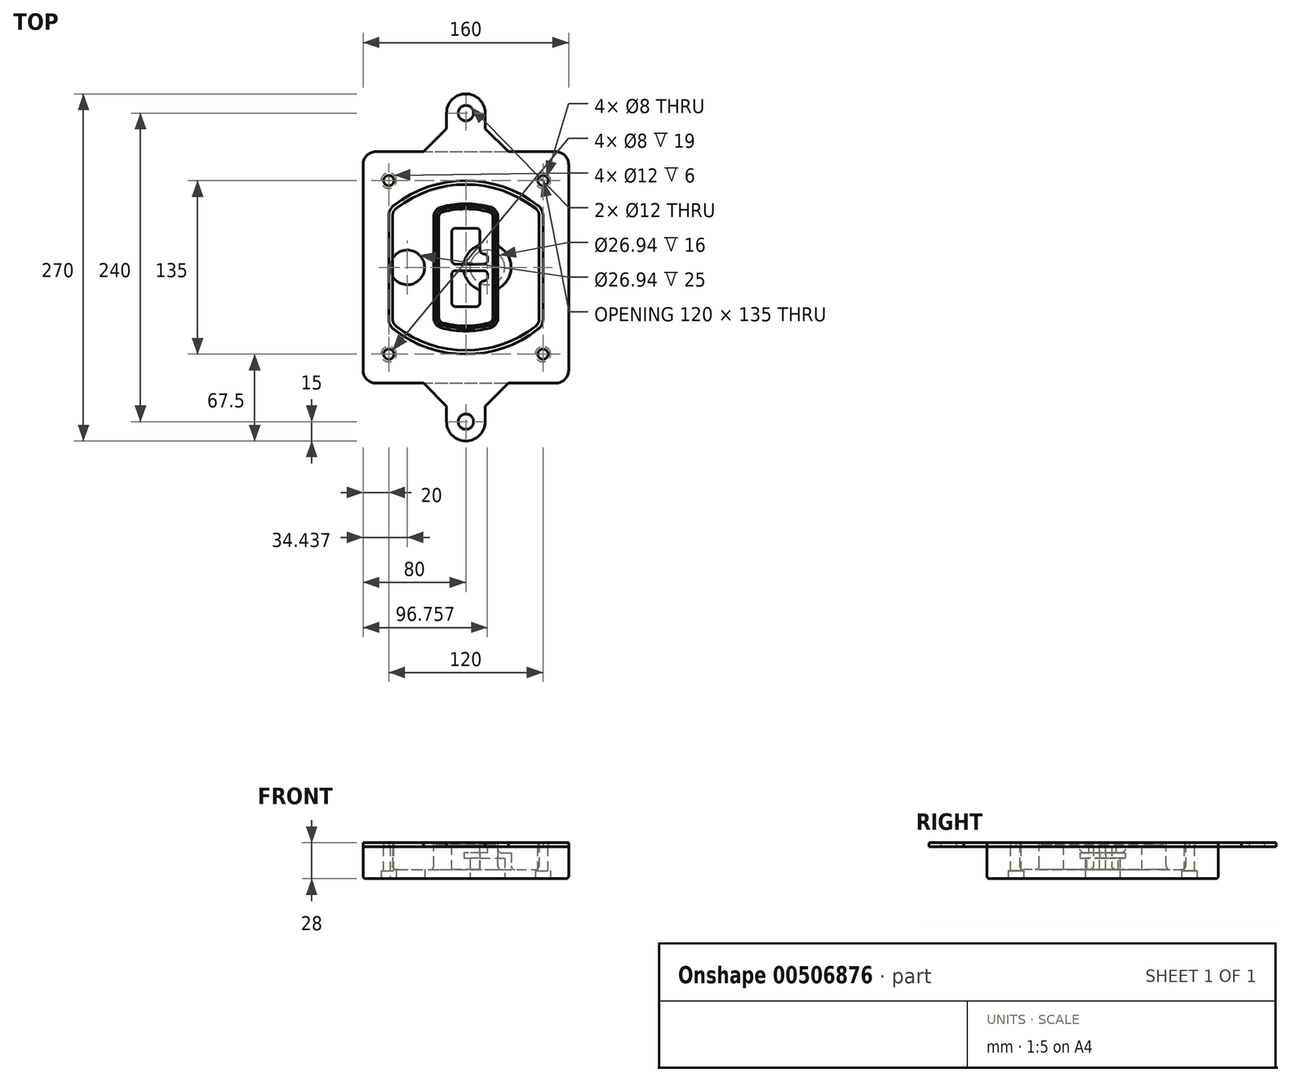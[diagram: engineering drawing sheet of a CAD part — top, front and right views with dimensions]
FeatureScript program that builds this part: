
annotation { "Feature Type Name" : "Feature", "Feature Type Description" : "" }
export const myFeature = defineFeature(function(context is Context, id is Id, definition is map)
    precondition{}
    {
        {
            var Q0;
            Q0=qCreatedBy(makeId("Top.planeOp"),FACE);
            var sketch = newSketch(context, id + "F0", { "sketchPlane" : qUnion([Q0])});
            skPoint(sketch, "E0.rect.middle", {"position": v(0, 0) * mm});
            skLineSegment(sketch, "E1.bottom", {"start": v(-70, -90) * mm, "end": v(70, -90) * mm});
            skLineSegment(sketch, "E1.top", {"start": v(-70, 90) * mm, "end": v(70, 90) * mm});
            skLineSegment(sketch, "E1.left", {"start": v(-80, -80) * mm, "end": v(-80, 80) * mm});
            skLineSegment(sketch, "E1.right", {"start": v(80, -80) * mm, "end": v(80, 80) * mm});
            skLineSegment(sketch, "E2", {"start": v(-80, 90) * mm, "end": v(80, -90) * mm, "construction": true});
            skLineSegment(sketch, "E3", {"start": v(80, 90) * mm, "end": v(-80, -90) * mm, "construction": true});
            skCircle(sketch, "E4", {"center": v(-60, 67.5) * mm, "radius": 4 * mm});
            skCircle(sketch, "E5", {"center": v(60, 67.5) * mm, "radius": 4 * mm});
            skCircle(sketch, "E6", {"center": v(60, -67.5) * mm, "radius": 4 * mm});
            skCircle(sketch, "E7", {"center": v(-60, -67.5) * mm, "radius": 4 * mm});
            skLineSegment(sketch, "E8", {"start": v(-60, 67.5) * mm, "end": v(60, 67.5) * mm, "construction": true});
            skLineSegment(sketch, "E9", {"start": v(60, 67.5) * mm, "end": v(60, -67.5) * mm, "construction": true});
            skLineSegment(sketch, "E10", {"start": v(60, -67.5) * mm, "end": v(-60, -67.5) * mm, "construction": true});
            skLineSegment(sketch, "E11", {"start": v(-60, -67.5) * mm, "end": v(-60, 67.5) * mm, "construction": true});
            skLineSegment(sketch, "E12", {"start": v(-60, 40.3) * mm, "end": v(-60, -40.3) * mm});
            skLineSegment(sketch, "E13", {"start": v(60, 40.3) * mm, "end": v(60, -40.3) * mm});
            skArc(sketch, "E14", {"start": v(56.15, 48.18) * mm, "mid": v(0, 67.5) * mm, "end": v(-56.15, 48.18) * mm});
            skArc(sketch, "E15", {"start": v(-56.15, -48.18) * mm, "mid": v(0, -67.5) * mm, "end": v(56.15, -48.18) * mm});
            skLineSegment(sketch, "E16", {"start": v(-60, 0) * mm, "end": v(60, 0) * mm, "construction": true});
            skPoint(sketch, "E17.visualSharp", {"position": v(-60, -45) * mm});
            skArc(sketch, "E17.filletArc", {"start": v(-60, -40.3) * mm, "mid": v(-58.99, -44.68) * mm, "end": v(-56.15, -48.18) * mm});
            skPoint(sketch, "E18.visualSharp", {"position": v(-60, 45) * mm});
            skArc(sketch, "E18.filletArc", {"start": v(-56.15, 48.18) * mm, "mid": v(-58.99, 44.68) * mm, "end": v(-60, 40.3) * mm});
            skPoint(sketch, "E19.visualSharp", {"position": v(60, 45) * mm});
            skArc(sketch, "E19.filletArc", {"start": v(60, 40.3) * mm, "mid": v(58.99, 44.68) * mm, "end": v(56.15, 48.18) * mm});
            skPoint(sketch, "E20.visualSharp", {"position": v(60, -45) * mm});
            skArc(sketch, "E20.filletArc", {"start": v(56.15, -48.18) * mm, "mid": v(58.99, -44.68) * mm, "end": v(60, -40.3) * mm});
            skPoint(sketch, "E21.visualSharp", {"position": v(-80, 90) * mm});
            skArc(sketch, "E21.filletArc", {"start": v(-70, 90) * mm, "mid": v(-77.07, 87.07) * mm, "end": v(-80, 80) * mm});
            skPoint(sketch, "E22.visualSharp", {"position": v(80, 90) * mm});
            skArc(sketch, "E22.filletArc", {"start": v(80, 80) * mm, "mid": v(77.07, 87.07) * mm, "end": v(70, 90) * mm});
            skPoint(sketch, "E23.visualSharp", {"position": v(80, -90) * mm});
            skArc(sketch, "E23.filletArc", {"start": v(70, -90) * mm, "mid": v(77.07, -87.07) * mm, "end": v(80, -80) * mm});
            skPoint(sketch, "E24.visualSharp", {"position": v(-80, -90) * mm});
            skArc(sketch, "E24.filletArc", {"start": v(-80, -80) * mm, "mid": v(-77.07, -87.07) * mm, "end": v(-70, -90) * mm});
            skArc(sketch, "E25.0", {"start": v(57, 40.3) * mm, "mid": v(56.3, 43.36) * mm, "end": v(54.3, 45.81) * mm});
            skLineSegment(sketch, "E25.1", {"start": v(57, 40.3) * mm, "end": v(57, -40.3) * mm});
            skArc(sketch, "E25.2", {"start": v(54.3, -45.81) * mm, "mid": v(56.3, -43.36) * mm, "end": v(57, -40.3) * mm});
            skArc(sketch, "E25.3", {"start": v(-54.3, -45.81) * mm, "mid": v(0, -64.5) * mm, "end": v(54.3, -45.81) * mm});
            skArc(sketch, "E25.4", {"start": v(-57, -40.3) * mm, "mid": v(-56.3, -43.36) * mm, "end": v(-54.3, -45.81) * mm});
            skArc(sketch, "E25.5", {"start": v(54.3, 45.81) * mm, "mid": v(0, 64.5) * mm, "end": v(-54.3, 45.81) * mm});
            skLineSegment(sketch, "E25.6", {"start": v(-57, 40.3) * mm, "end": v(-57, -40.3) * mm});
            skArc(sketch, "E25.7", {"start": v(-54.3, 45.81) * mm, "mid": v(-56.3, 43.36) * mm, "end": v(-57, 40.3) * mm});
            skArc(sketch, "E26.0", {"start": v(-58.62, 51.33) * mm, "mid": v(-62.58, 46.43) * mm, "end": v(-64, 40.3) * mm});
            skArc(sketch, "E26.1", {"start": v(58.62, 51.33) * mm, "mid": v(0, 71.5) * mm, "end": v(-58.62, 51.33) * mm});
            skArc(sketch, "E26.2", {"start": v(64, 40.3) * mm, "mid": v(62.58, 46.43) * mm, "end": v(58.62, 51.33) * mm});
            skLineSegment(sketch, "E26.3", {"start": v(64, 40.3) * mm, "end": v(64, -40.3) * mm});
            skArc(sketch, "E26.4", {"start": v(58.62, -51.33) * mm, "mid": v(62.58, -46.43) * mm, "end": v(64, -40.3) * mm});
            skLineSegment(sketch, "E26.5", {"start": v(-64, 40.3) * mm, "end": v(-64, -40.3) * mm});
            skArc(sketch, "E26.6", {"start": v(-58.62, -51.33) * mm, "mid": v(0, -71.5) * mm, "end": v(58.62, -51.33) * mm});
            skArc(sketch, "E26.7", {"start": v(-64, -40.3) * mm, "mid": v(-62.58, -46.43) * mm, "end": v(-58.62, -51.33) * mm});
            skSolve(sketch);
        }
        {
            var Q0;
            Q0=makeQuery(id+"F0.imprint","IMPRINT",FACE,{"disambiguationData":[TD([[makeQuery(id+"F0.imprint","IMPRINT",EDGE,{"derivedFrom":sQuery(id+"F0.wireOp",EDGE,"E1.bottom")}),1.0]])]});
            var Q1;
            Q1=makeQuery(id+"F0.imprint","IMPRINT",FACE,{"disambiguationData":[TD([[makeQuery(id+"F0.imprint","IMPRINT",EDGE,{"derivedFrom":sQuery(id+"F0.wireOp",EDGE,"E12")}),1.0]])]});
            var Q2;
            Q2=makeQuery(id+"F0.imprint","IMPRINT",FACE,{"disambiguationData":[TD([[makeQuery(id+"F0.imprint","IMPRINT",EDGE,{"derivedFrom":sQuery(id+"F0.wireOp",EDGE,"E25.0")}),1.0]])]});
            var Q3;
            Q3=makeQuery(id+"F0.imprint","IMPRINT",FACE,{"disambiguationData":[TD([[makeQuery(id+"F0.imprint","IMPRINT",EDGE,{"derivedFrom":sQuery(id+"F0.wireOp",EDGE,"E12")}),-1.0]])]});
            extrude(context, id + "F1", {"entities" : qUnion([Q0, Q1, Q2, Q3]), "oppositeDirection" : true, "depth" : 25 * mm});
        }
        {
            var Q0;
            Q0=makeQuery(id+"F0.imprint","IMPRINT",FACE,{"disambiguationData":[TD([[makeQuery(id+"F0.imprint","IMPRINT",EDGE,{"derivedFrom":sQuery(id+"F0.wireOp",EDGE,"E12")}),1.0]])]});
            extrude(context, id + "F2", {"entities" : qUnion([Q0]), "operationType" : NewBodyOperationType.ADD, "depth" : 3 * mm});
        }
        {
            var Q0;
            Q0=makeQuery(id+"F0.imprint","IMPRINT",FACE,{"disambiguationData":[TD([[makeQuery(id+"F0.imprint","IMPRINT",EDGE,{"derivedFrom":sQuery(id+"F0.wireOp",EDGE,"E25.0")}),1.0]])]});
            extrude(context, id + "F3", {"entities" : qUnion([Q0]), "operationType" : NewBodyOperationType.REMOVE, "oppositeDirection" : true, "depth" : 18 * mm});
        }
        {
            var Q0;
            Q0=makeQuery(id+"F2.opExtrude","CAP_FACE",FACE,{"disambiguationData":[OSD([sQuery(id+"F0.wireOp",EDGE,"E12"),sQuery(id+"F0.wireOp",EDGE,"E13"),sQuery(id+"F0.wireOp",EDGE,"E14"),sQuery(id+"F0.wireOp",EDGE,"E15"),sQuery(id+"F0.wireOp",EDGE,"E17.filletArc"),sQuery(id+"F0.wireOp",EDGE,"E18.filletArc"),sQuery(id+"F0.wireOp",EDGE,"E19.filletArc"),sQuery(id+"F0.wireOp",EDGE,"E20.filletArc"),sQuery(id+"F0.wireOp",EDGE,"E25.0"),sQuery(id+"F0.wireOp",EDGE,"E25.1"),sQuery(id+"F0.wireOp",EDGE,"E25.2"),sQuery(id+"F0.wireOp",EDGE,"E25.3"),sQuery(id+"F0.wireOp",EDGE,"E25.4"),sQuery(id+"F0.wireOp",EDGE,"E25.5"),sQuery(id+"F0.wireOp",EDGE,"E25.6"),sQuery(id+"F0.wireOp",EDGE,"E25.7")])],"isStart":false});
            var sketch = newSketch(context, id + "F4", { "sketchPlane" : qUnion([Q0])});
            skArc(sketch, "E27.0", {"start": v(-19.08, -46.97) * mm, "mid": v(0, -49.5) * mm, "end": v(19.08, -46.97) * mm});
            skArc(sketch, "E28.0", {"start": v(19.08, 46.97) * mm, "mid": v(0, 49.5) * mm, "end": v(-19.08, 46.97) * mm});
            skLineSegment(sketch, "E29", {"start": v(-25, 39.25) * mm, "end": v(-25, -39.25) * mm});
            skLineSegment(sketch, "E30", {"start": v(25, 39.25) * mm, "end": v(25, -39.25) * mm});
            skLineSegment(sketch, "E31", {"start": v(-25, 45.1) * mm, "end": v(25, 45.1) * mm, "construction": true});
            skLineSegment(sketch, "E32", {"start": v(-25, -45.1) * mm, "end": v(25, -45.1) * mm, "construction": true});
            skPoint(sketch, "E33.visualSharp", {"position": v(-25, 45.1) * mm});
            skArc(sketch, "E33.filletArc", {"start": v(-19.08, 46.97) * mm, "mid": v(-23.35, 44.11) * mm, "end": v(-25, 39.25) * mm});
            skPoint(sketch, "E34.visualSharp", {"position": v(25, 45.1) * mm});
            skArc(sketch, "E34.filletArc", {"start": v(25, 39.25) * mm, "mid": v(23.35, 44.11) * mm, "end": v(19.08, 46.97) * mm});
            skPoint(sketch, "E35.visualSharp", {"position": v(25, -45.1) * mm});
            skArc(sketch, "E35.filletArc", {"start": v(19.08, -46.97) * mm, "mid": v(23.35, -44.11) * mm, "end": v(25, -39.25) * mm});
            skPoint(sketch, "E36.visualSharp", {"position": v(-25, -45.1) * mm});
            skArc(sketch, "E36.filletArc", {"start": v(-25, -39.25) * mm, "mid": v(-23.35, -44.11) * mm, "end": v(-19.08, -46.97) * mm});
            skArc(sketch, "E37.0", {"start": v(54.3, 45.81) * mm, "mid": v(0, 64.5) * mm, "end": v(-54.3, 45.81) * mm});
            skArc(sketch, "E37.1", {"start": v(-54.3, 45.81) * mm, "mid": v(-56.3, 43.36) * mm, "end": v(-57, 40.3) * mm});
            skLineSegment(sketch, "E37.2", {"start": v(-57, 40.3) * mm, "end": v(-57, -40.3) * mm});
            skArc(sketch, "E37.3", {"start": v(-57, -40.3) * mm, "mid": v(-56.3, -43.36) * mm, "end": v(-54.3, -45.81) * mm});
            skArc(sketch, "E37.4", {"start": v(-54.3, -45.81) * mm, "mid": v(0, -64.5) * mm, "end": v(54.3, -45.81) * mm});
            skArc(sketch, "E37.5", {"start": v(54.3, -45.81) * mm, "mid": v(56.3, -43.36) * mm, "end": v(57, -40.3) * mm});
            skLineSegment(sketch, "E37.6", {"start": v(57, 40.3) * mm, "end": v(57, -40.3) * mm});
            skArc(sketch, "E37.7", {"start": v(57, 40.3) * mm, "mid": v(56.3, 43.36) * mm, "end": v(54.3, 45.81) * mm});
            skLineSegment(sketch, "E38.0", {"start": v(23, 39.25) * mm, "end": v(23, -39.25) * mm});
            skArc(sketch, "E38.1", {"start": v(18.56, -45.04) * mm, "mid": v(21.76, -42.9) * mm, "end": v(23, -39.25) * mm});
            skArc(sketch, "E38.2", {"start": v(-18.56, -45.04) * mm, "mid": v(0, -47.5) * mm, "end": v(18.56, -45.04) * mm});
            skArc(sketch, "E38.3", {"start": v(-23, -39.25) * mm, "mid": v(-21.76, -42.9) * mm, "end": v(-18.56, -45.04) * mm});
            skLineSegment(sketch, "E38.4", {"start": v(-23, 39.25) * mm, "end": v(-23, -39.25) * mm});
            skArc(sketch, "E38.5", {"start": v(23, 39.25) * mm, "mid": v(21.76, 42.9) * mm, "end": v(18.56, 45.04) * mm});
            skArc(sketch, "E38.6", {"start": v(-18.56, 45.04) * mm, "mid": v(-21.76, 42.9) * mm, "end": v(-23, 39.25) * mm});
            skArc(sketch, "E38.7", {"start": v(18.56, 45.04) * mm, "mid": v(0, 47.5) * mm, "end": v(-18.56, 45.04) * mm});
            skArc(sketch, "E39.0", {"start": v(21, 39.25) * mm, "mid": v(20.18, 41.68) * mm, "end": v(18.04, 43.1) * mm});
            skLineSegment(sketch, "E39.1", {"start": v(21, 39.25) * mm, "end": v(21, -39.25) * mm});
            skArc(sketch, "E39.2", {"start": v(18.04, -43.1) * mm, "mid": v(20.18, -41.68) * mm, "end": v(21, -39.25) * mm});
            skArc(sketch, "E39.3", {"start": v(-18.04, -43.1) * mm, "mid": v(0, -45.5) * mm, "end": v(18.04, -43.1) * mm});
            skArc(sketch, "E39.4", {"start": v(-21, -39.25) * mm, "mid": v(-20.18, -41.68) * mm, "end": v(-18.04, -43.1) * mm});
            skArc(sketch, "E39.5", {"start": v(18.04, 43.1) * mm, "mid": v(0, 45.5) * mm, "end": v(-18.04, 43.1) * mm});
            skLineSegment(sketch, "E39.6", {"start": v(-21, 39.25) * mm, "end": v(-21, -39.25) * mm});
            skArc(sketch, "E39.7", {"start": v(-18.04, 43.1) * mm, "mid": v(-20.18, 41.68) * mm, "end": v(-21, 39.25) * mm});
            skLineSegment(sketch, "E40", {"start": v(-25, 0) * mm, "end": v(25, 0) * mm, "construction": true});
            skLineSegment(sketch, "E41", {"start": v(-11, 5.5) * mm, "end": v(-11, 27.5) * mm});
            skLineSegment(sketch, "E42", {"start": v(-8, 30.5) * mm, "end": v(8, 30.5) * mm});
            skLineSegment(sketch, "E43", {"start": v(11, 27.5) * mm, "end": v(11, 13.5) * mm});
            skLineSegment(sketch, "E44", {"start": v(14, 10.5) * mm, "end": v(14, 10.5) * mm});
            skLineSegment(sketch, "E45", {"start": v(17, 7.5) * mm, "end": v(17, 5.5) * mm});
            skLineSegment(sketch, "E46", {"start": v(14, 2.5) * mm, "end": v(-8, 2.5) * mm});
            skPoint(sketch, "E47.visualSharp", {"position": v(-11, 30.5) * mm});
            skArc(sketch, "E47.filletArc", {"start": v(-8, 30.5) * mm, "mid": v(-10.12, 29.62) * mm, "end": v(-11, 27.5) * mm});
            skPoint(sketch, "E48.visualSharp", {"position": v(11, 30.5) * mm});
            skArc(sketch, "E48.filletArc", {"start": v(11, 27.5) * mm, "mid": v(10.12, 29.62) * mm, "end": v(8, 30.5) * mm});
            skPoint(sketch, "E49.visualSharp", {"position": v(11, 10.5) * mm});
            skArc(sketch, "E49.filletArc", {"start": v(11, 13.5) * mm, "mid": v(11.88, 11.38) * mm, "end": v(14, 10.5) * mm});
            skPoint(sketch, "E50.visualSharp", {"position": v(17, 10.5) * mm});
            skArc(sketch, "E50.filletArc", {"start": v(17, 7.5) * mm, "mid": v(16.12, 9.62) * mm, "end": v(14, 10.5) * mm});
            skPoint(sketch, "E51.visualSharp", {"position": v(17, 2.5) * mm});
            skArc(sketch, "E51.filletArc", {"start": v(14, 2.5) * mm, "mid": v(16.12, 3.38) * mm, "end": v(17, 5.5) * mm});
            skPoint(sketch, "E52.visualSharp", {"position": v(-11, 2.5) * mm});
            skArc(sketch, "E52.filletArc", {"start": v(-11, 5.5) * mm, "mid": v(-10.12, 3.38) * mm, "end": v(-8, 2.5) * mm});
            skLineSegment(sketch, "E53.0.MirrorCS", {"start": v(14, -2.5) * mm, "end": v(-8, -2.5) * mm});
            skArc(sketch, "E54.0.MirrorCS", {"start": v(-11, -5.5) * mm, "mid": v(-10.12, -3.38) * mm, "end": v(-8, -2.5) * mm});
            skLineSegment(sketch, "E55.0.MirrorCS", {"start": v(-11, -5.5) * mm, "end": v(-11, -27.5) * mm});
            skArc(sketch, "E56.0.MirrorCS", {"start": v(-8, -30.5) * mm, "mid": v(-10.12, -29.62) * mm, "end": v(-11, -27.5) * mm});
            skLineSegment(sketch, "E57.0.MirrorCS", {"start": v(-8, -30.5) * mm, "end": v(8, -30.5) * mm});
            skArc(sketch, "E58.0.MirrorCS", {"start": v(11, -27.5) * mm, "mid": v(10.12, -29.62) * mm, "end": v(8, -30.5) * mm});
            skLineSegment(sketch, "E59.0.MirrorCS", {"start": v(11, -27.5) * mm, "end": v(11, -13.5) * mm});
            skArc(sketch, "E60.0.MirrorCS", {"start": v(11, -13.5) * mm, "mid": v(11.88, -11.38) * mm, "end": v(14, -10.5) * mm});
            skArc(sketch, "E61.0.MirrorCS", {"start": v(17, -7.5) * mm, "mid": v(16.12, -9.62) * mm, "end": v(14, -10.5) * mm});
            skLineSegment(sketch, "E62.0.MirrorCS", {"start": v(17, -7.5) * mm, "end": v(17, -5.5) * mm});
            skArc(sketch, "E63.0.MirrorCS", {"start": v(14, -2.5) * mm, "mid": v(16.12, -3.38) * mm, "end": v(17, -5.5) * mm});
            skSolve(sketch);
        }
        {
            var Q0;
            Q0=makeQuery(id+"F4.imprint","IMPRINT",FACE,{"disambiguationData":[TD([[makeQuery(id+"F4.imprint","IMPRINT",EDGE,{"derivedFrom":sQuery(id+"F4.wireOp",EDGE,"E27.0")}),1.0]])]});
            var Q1;
            Q1=makeQuery(id+"F4.imprint","IMPRINT",FACE,{"disambiguationData":[TD([[makeQuery(id+"F4.imprint","IMPRINT",EDGE,{"derivedFrom":sQuery(id+"F4.wireOp",EDGE,"E38.0")}),-1.0]])]});
            var Q2;
            Q2=makeQuery(id+"F4.imprint","IMPRINT",FACE,{"disambiguationData":[TD([[makeQuery(id+"F4.imprint","IMPRINT",EDGE,{"derivedFrom":sQuery(id+"F4.wireOp",EDGE,"E39.0")}),1.0]])]});
            extrude(context, id + "F5", {"entities" : qUnion([Q0, Q1, Q2]), "operationType" : NewBodyOperationType.ADD, "endBound" : BoundingType.UP_TO_NEXT, "oppositeDirection" : true, "depth" : 25 * mm});
        }
        {
            var Q0;
            Q0=makeQuery(id+"F4.imprint","IMPRINT",FACE,{"disambiguationData":[TD([[makeQuery(id+"F4.imprint","IMPRINT",EDGE,{"derivedFrom":sQuery(id+"F4.wireOp",EDGE,"E38.0")}),-1.0]])]});
            extrude(context, id + "F6", {"entities" : qUnion([Q0]), "operationType" : NewBodyOperationType.REMOVE, "oppositeDirection" : true, "depth" : 2 * mm});
        }
        {
            var Q0;
            Q0=makeQuery(id+"F1.opExtrude","CAP_FACE",FACE,{"disambiguationData":[OSD([sQuery(id+"F0.wireOp",EDGE,"E1.bottom"),sQuery(id+"F0.wireOp",EDGE,"E1.top"),sQuery(id+"F0.wireOp",EDGE,"E1.left"),sQuery(id+"F0.wireOp",EDGE,"E1.right"),sQuery(id+"F0.wireOp",EDGE,"E4"),sQuery(id+"F0.wireOp",EDGE,"E5"),sQuery(id+"F0.wireOp",EDGE,"E6"),sQuery(id+"F0.wireOp",EDGE,"E7"),sQuery(id+"F0.wireOp",EDGE,"E21.filletArc"),sQuery(id+"F0.wireOp",EDGE,"E22.filletArc"),sQuery(id+"F0.wireOp",EDGE,"E23.filletArc"),sQuery(id+"F0.wireOp",EDGE,"E24.filletArc")])],"isStart":false});
            var sketch = newSketch(context, id + "F7", { "sketchPlane" : qUnion([Q0])});
            skCircle(sketch, "E64", {"center": v(16.76, 0) * mm, "radius": 13.47 * mm});
            skCircle(sketch, "E65", {"center": v(-45.56, 0) * mm, "radius": 13.47 * mm});
            skLineSegment(sketch, "E66", {"start": v(80, 0) * mm, "end": v(-80, 0) * mm});
            skCircle(sketch, "E67", {"center": v(16.76, 0) * mm, "radius": 18.47 * mm});
            skCircle(sketch, "E68", {"center": v(60, -67.5) * mm, "radius": 6 * mm});
            skCircle(sketch, "E69", {"center": v(-60, -67.5) * mm, "radius": 6 * mm});
            skCircle(sketch, "E70", {"center": v(-60, 67.5) * mm, "radius": 6 * mm});
            skCircle(sketch, "E71", {"center": v(60, 67.5) * mm, "radius": 6 * mm});
            skSolve(sketch);
        }
        {
            var Q0;
            {var subQ1=sQuery(id+"F7.wireOp",EDGE,"E66");var subQ4=sQuery(id+"F7.wireOp",EDGE,"E64");var subQ6=makeQuery(id+"F7.imprint","INTERSECT",VERTEX,{"disambiguationData":[OD(0.0)],"derivedFrom":[subQ4,subQ1]});Q0=makeQuery(id+"F7.imprint","IMPRINT",FACE,{"disambiguationData":[TD([[makeQuery(id+"F7.imprint","IMPRINT",EDGE,{"disambiguationData":[TD([[subQ6,-1.0]])],"derivedFrom":subQ4}),-1.0]])]});}
            var Q1;
            {var subQ0=sQuery(id+"F7.wireOp",EDGE,"E66");var subQ1=sQuery(id+"F7.wireOp",EDGE,"E64");var subQ3=makeQuery(id+"F7.imprint","INTERSECT",VERTEX,{"disambiguationData":[OD(0.0)],"derivedFrom":[subQ1,subQ0]});Q1=makeQuery(id+"F7.imprint","IMPRINT",FACE,{"disambiguationData":[TD([[makeQuery(id+"F7.imprint","IMPRINT",EDGE,{"disambiguationData":[TD([[subQ3,-1.0]])],"derivedFrom":subQ1}),1.0]])]});}
            var Q2;
            {var subQ0=sQuery(id+"F7.wireOp",EDGE,"E66");var subQ1=sQuery(id+"F7.wireOp",EDGE,"E64");var subQ3=makeQuery(id+"F7.imprint","INTERSECT",VERTEX,{"disambiguationData":[OD(0.0)],"derivedFrom":[subQ1,subQ0]});Q2=makeQuery(id+"F7.imprint","IMPRINT",FACE,{"disambiguationData":[TD([[makeQuery(id+"F7.imprint","IMPRINT",EDGE,{"disambiguationData":[TD([[subQ3,1.0]])],"derivedFrom":subQ1}),1.0]])]});}
            var Q3;
            {var subQ1=sQuery(id+"F7.wireOp",EDGE,"E66");var subQ4=sQuery(id+"F7.wireOp",EDGE,"E64");var subQ6=makeQuery(id+"F7.imprint","INTERSECT",VERTEX,{"disambiguationData":[OD(0.0)],"derivedFrom":[subQ4,subQ1]});Q3=makeQuery(id+"F7.imprint","IMPRINT",FACE,{"disambiguationData":[TD([[makeQuery(id+"F7.imprint","IMPRINT",EDGE,{"disambiguationData":[TD([[subQ6,1.0]])],"derivedFrom":subQ4}),-1.0]])]});}
            extrude(context, id + "F8", {"entities" : qUnion([Q0, Q1, Q2, Q3]), "operationType" : NewBodyOperationType.ADD, "oppositeDirection" : true, "depth" : 20 * mm});
        }
        {
            var Q0;
            {var subQ0=sQuery(id+"F7.wireOp",EDGE,"E66");var subQ1=sQuery(id+"F7.wireOp",EDGE,"E64");var subQ3=makeQuery(id+"F7.imprint","INTERSECT",VERTEX,{"disambiguationData":[OD(0.0)],"derivedFrom":[subQ1,subQ0]});Q0=makeQuery(id+"F7.imprint","IMPRINT",FACE,{"disambiguationData":[TD([[makeQuery(id+"F7.imprint","IMPRINT",EDGE,{"disambiguationData":[TD([[subQ3,-1.0]])],"derivedFrom":subQ1}),1.0]])]});}
            var Q1;
            {var subQ0=sQuery(id+"F7.wireOp",EDGE,"E66");var subQ1=sQuery(id+"F7.wireOp",EDGE,"E64");var subQ3=makeQuery(id+"F7.imprint","INTERSECT",VERTEX,{"disambiguationData":[OD(0.0)],"derivedFrom":[subQ1,subQ0]});Q1=makeQuery(id+"F7.imprint","IMPRINT",FACE,{"disambiguationData":[TD([[makeQuery(id+"F7.imprint","IMPRINT",EDGE,{"disambiguationData":[TD([[subQ3,1.0]])],"derivedFrom":subQ1}),1.0]])]});}
            extrude(context, id + "F9", {"entities" : qUnion([Q0, Q1]), "operationType" : NewBodyOperationType.REMOVE, "oppositeDirection" : true, "depth" : 16 * mm});
        }
        {
            var Q0;
            {var subQ0=sQuery(id+"F7.wireOp",EDGE,"E66");var subQ1=sQuery(id+"F7.wireOp",EDGE,"E65");var subQ3=makeQuery(id+"F7.imprint","INTERSECT",VERTEX,{"disambiguationData":[OD(0.0)],"derivedFrom":[subQ1,subQ0]});Q0=makeQuery(id+"F7.imprint","IMPRINT",FACE,{"disambiguationData":[TD([[makeQuery(id+"F7.imprint","IMPRINT",EDGE,{"disambiguationData":[TD([[subQ3,-1.0]])],"derivedFrom":subQ1}),1.0]])]});}
            var Q1;
            {var subQ0=sQuery(id+"F7.wireOp",EDGE,"E66");var subQ1=sQuery(id+"F7.wireOp",EDGE,"E65");var subQ3=makeQuery(id+"F7.imprint","INTERSECT",VERTEX,{"disambiguationData":[OD(0.0)],"derivedFrom":[subQ1,subQ0]});Q1=makeQuery(id+"F7.imprint","IMPRINT",FACE,{"disambiguationData":[TD([[makeQuery(id+"F7.imprint","IMPRINT",EDGE,{"disambiguationData":[TD([[subQ3,1.0]])],"derivedFrom":subQ1}),1.0]])]});}
            extrude(context, id + "F10", {"entities" : qUnion([Q0, Q1]), "operationType" : NewBodyOperationType.REMOVE, "oppositeDirection" : true, "depth" : 25 * mm});
        }
        {
            var Q0;
            Q0=makeQuery(id+"F7.imprint","IMPRINT",FACE,{"disambiguationData":[TD([[makeQuery(id+"F7.imprint","IMPRINT",EDGE,{"derivedFrom":sQuery(id+"F7.wireOp",EDGE,"E68")}),1.0]])]});
            var Q1;
            Q1=makeQuery(id+"F7.imprint","IMPRINT",FACE,{"disambiguationData":[TD([[makeQuery(id+"F7.imprint","IMPRINT",EDGE,{"derivedFrom":makeQuery(id+"F1.opExtrude","CAP_EDGE",EDGE,{"disambiguationData":[OSD([sQuery(id+"F0.wireOp",EDGE,"E5")])],"isStart":false})}),-1.0]])]});
            var Q2;
            Q2=makeQuery(id+"F7.imprint","IMPRINT",FACE,{"disambiguationData":[TD([[makeQuery(id+"F7.imprint","IMPRINT",EDGE,{"derivedFrom":sQuery(id+"F7.wireOp",EDGE,"E69")}),1.0]])]});
            var Q3;
            Q3=makeQuery(id+"F7.imprint","IMPRINT",FACE,{"disambiguationData":[TD([[makeQuery(id+"F7.imprint","IMPRINT",EDGE,{"derivedFrom":makeQuery(id+"F1.opExtrude","CAP_EDGE",EDGE,{"disambiguationData":[OSD([sQuery(id+"F0.wireOp",EDGE,"E4")])],"isStart":false})}),-1.0]])]});
            var Q4;
            Q4=makeQuery(id+"F7.imprint","IMPRINT",FACE,{"disambiguationData":[TD([[makeQuery(id+"F7.imprint","IMPRINT",EDGE,{"derivedFrom":sQuery(id+"F7.wireOp",EDGE,"E70")}),1.0]])]});
            var Q5;
            Q5=makeQuery(id+"F7.imprint","IMPRINT",FACE,{"disambiguationData":[TD([[makeQuery(id+"F7.imprint","IMPRINT",EDGE,{"derivedFrom":makeQuery(id+"F1.opExtrude","CAP_EDGE",EDGE,{"disambiguationData":[OSD([sQuery(id+"F0.wireOp",EDGE,"E7")])],"isStart":false})}),-1.0]])]});
            var Q6;
            Q6=makeQuery(id+"F7.imprint","IMPRINT",FACE,{"disambiguationData":[TD([[makeQuery(id+"F7.imprint","IMPRINT",EDGE,{"derivedFrom":sQuery(id+"F7.wireOp",EDGE,"E71")}),1.0]])]});
            var Q7;
            Q7=makeQuery(id+"F7.imprint","IMPRINT",FACE,{"disambiguationData":[TD([[makeQuery(id+"F7.imprint","IMPRINT",EDGE,{"derivedFrom":makeQuery(id+"F1.opExtrude","CAP_EDGE",EDGE,{"disambiguationData":[OSD([sQuery(id+"F0.wireOp",EDGE,"E6")])],"isStart":false})}),-1.0]])]});
            extrude(context, id + "F11", {"entities" : qUnion([Q0, Q1, Q2, Q3, Q4, Q5, Q6, Q7]), "operationType" : NewBodyOperationType.REMOVE, "oppositeDirection" : true, "depth" : 6 * mm});
        }
        {
            var Q0;
            Q0=makeQuery(id+"F9.boolean.opBoolean","COPY",FACE,{"derivedFrom":makeQuery(id+"F9.opExtrude","CAP_FACE",FACE,{"disambiguationData":[OSD([sQuery(id+"F7.wireOp",EDGE,"E64")])],"isStart":false})});
            var sketch = newSketch(context, id + "F12", { "sketchPlane" : qUnion([Q0])});
            skArc(sketch, "E72.0", {"start": v(11, 17.55) * mm, "mid": v(2.57, 11.82) * mm, "end": v(-1.54, 2.5) * mm});
            skArc(sketch, "E72.1", {"start": v(-1.54, -2.5) * mm, "mid": v(2.57, -11.82) * mm, "end": v(11, -17.55) * mm});
            skLineSegment(sketch, "E73", {"start": v(-1.54, -2.5) * mm, "end": v(14, -2.5) * mm});
            skLineSegment(sketch, "E74.0", {"start": v(14, 2.5) * mm, "end": v(-1.54, 2.5) * mm});
            skArc(sketch, "E74.1", {"start": v(14, 2.5) * mm, "mid": v(16.12, 3.38) * mm, "end": v(17, 5.5) * mm});
            skLineSegment(sketch, "E74.2", {"start": v(17, 7.5) * mm, "end": v(17, 5.5) * mm});
            skArc(sketch, "E74.3", {"start": v(17, 7.5) * mm, "mid": v(16.12, 9.62) * mm, "end": v(14, 10.5) * mm});
            skArc(sketch, "E74.4", {"start": v(11, 13.5) * mm, "mid": v(11.88, 11.38) * mm, "end": v(14, 10.5) * mm});
            skLineSegment(sketch, "E74.5", {"start": v(11, 17.55) * mm, "end": v(11, 13.5) * mm});
            skLineSegment(sketch, "E74.7", {"start": v(14, -2.5) * mm, "end": v(-1.54, -2.5) * mm});
            skArc(sketch, "E74.8", {"start": v(14, -2.5) * mm, "mid": v(16.12, -3.38) * mm, "end": v(17, -5.5) * mm});
            skLineSegment(sketch, "E74.9", {"start": v(17, -7.5) * mm, "end": v(17, -5.5) * mm});
            skArc(sketch, "E74.10", {"start": v(17, -7.5) * mm, "mid": v(16.12, -9.62) * mm, "end": v(14, -10.5) * mm});
            skArc(sketch, "E74.11", {"start": v(11, -13.5) * mm, "mid": v(11.88, -11.38) * mm, "end": v(14, -10.5) * mm});
            skLineSegment(sketch, "E74.12", {"start": v(11, -17.55) * mm, "end": v(11, -13.5) * mm});
            skPoint(sketch, "E75.orphan", {"position": v(11, -27.5) * mm});
            skPoint(sketch, "E76.orphan", {"position": v(-8, -2.5) * mm});
            skPoint(sketch, "E77.orphan", {"position": v(-8, 2.5) * mm});
            skPoint(sketch, "E78.orphan", {"position": v(11, 27.5) * mm});
            skSolve(sketch);
        }
        {
            var Q0;
            {var subQ7=sQuery(id+"F12.wireOp",EDGE,"E72.0");var subQ14=sQuery(id+"F12.wireOp",EDGE,"E72.1");var subQ16=sQuery(id+"F12.wireOp",EDGE,"E74.1");var subQ18=sQuery(id+"F12.wireOp",EDGE,"E74.8");Q0=qUnion([makeQuery(id+"F12.imprint","IMPRINT",FACE,{"disambiguationData":[TD([[makeQuery(id+"F12.imprint","IMPRINT",EDGE,{"derivedFrom":subQ7}),1.0]])]}),makeQuery(id+"F12.imprint","IMPRINT",FACE,{"disambiguationData":[TD([[makeQuery(id+"F12.imprint","IMPRINT",EDGE,{"derivedFrom":subQ14}),1.0]])]}),makeQuery(id+"F12.imprint","IMPRINT",FACE,{"disambiguationData":[TD([[makeQuery(id+"F12.imprint","IMPRINT",EDGE,{"derivedFrom":subQ16}),1.0]])]}),makeQuery(id+"F12.imprint","IMPRINT",FACE,{"disambiguationData":[TD([[makeQuery(id+"F12.imprint","IMPRINT",EDGE,{"derivedFrom":subQ18}),-1.0]])]})]);}
            var Q1;
            Q1=makeQuery(id+"F5.boolean.opBoolean","SPLIT",FACE,{"disambiguationData":[TD([makeQuery(id+"F5.opExtrude","SWEPT_FACE",FACE,{"disambiguationData":[OSD([sQuery(id+"F4.wireOp",EDGE,"E41")])]})])],"derivedFrom":makeQuery(id+"F3.boolean.opBoolean","COPY",FACE,{"derivedFrom":makeQuery(id+"F3.opExtrude","CAP_FACE",FACE,{"disambiguationData":[OSD([sQuery(id+"F0.wireOp",EDGE,"E25.0"),sQuery(id+"F0.wireOp",EDGE,"E25.1"),sQuery(id+"F0.wireOp",EDGE,"E25.2"),sQuery(id+"F0.wireOp",EDGE,"E25.3"),sQuery(id+"F0.wireOp",EDGE,"E25.4"),sQuery(id+"F0.wireOp",EDGE,"E25.5"),sQuery(id+"F0.wireOp",EDGE,"E25.6"),sQuery(id+"F0.wireOp",EDGE,"E25.7")])],"isStart":false})})});
            extrude(context, id + "F13", {"entities" : qUnion([Q0]), "operationType" : NewBodyOperationType.REMOVE, "endBound" : BoundingType.UP_TO_SURFACE, "endBoundEntityFace" : qUnion([Q1]), "depth" : 25 * mm});
        }
        {
            var Q0;
            Q0=makeQuery(id+"F3.boolean.opBoolean","COPY",EDGE,{"derivedFrom":makeQuery(id+"F3.opExtrude","CAP_EDGE",EDGE,{"disambiguationData":[OSD([sQuery(id+"F0.wireOp",EDGE,"E25.6")])],"isStart":false})});
            var Q1;
            Q1=makeQuery(id+"F8.boolean.opBoolean","INTERSECT",EDGE,{"derivedFrom":[makeQuery(id+"F5.opExtrude","SWEPT_FACE",FACE,{"disambiguationData":[OSD([sQuery(id+"F4.wireOp",EDGE,"E30")])]}),makeQuery(id+"F8.opExtrude","CAP_FACE",FACE,{"disambiguationData":[OSD([sQuery(id+"F7.wireOp",EDGE,"E67")])],"isStart":false})]});
            var Q2;
            Q2=makeQuery(id+"F8.boolean.opBoolean","INTERSECT",EDGE,{"disambiguationData":[OD(1.0)],"derivedFrom":[makeQuery(id+"F5.opExtrude","SWEPT_FACE",FACE,{"disambiguationData":[OSD([sQuery(id+"F4.wireOp",EDGE,"E30")])]}),makeQuery(id+"F8.opExtrude","SWEPT_FACE",FACE,{"disambiguationData":[OSD([sQuery(id+"F7.wireOp",EDGE,"E67")])]})]});
            var Q3;
            {var subQ0=sQuery(id+"F4.wireOp",EDGE,"E30");Q3=makeQuery(id+"F8.boolean.opBoolean","SPLIT",EDGE,{"disambiguationData":[TD([makeQuery(id+"F5.opExtrude","SWEPT_FACE",FACE,{"disambiguationData":[OSD([sQuery(id+"F4.wireOp",EDGE,"E35.filletArc")])]})])],"derivedFrom":makeQuery(id+"F5.opExtrude","CAP_EDGE",EDGE,{"disambiguationData":[OSD([subQ0])],"isStart":false})});}
            var Q4;
            {var subQ0=sQuery(id+"F0.wireOp",EDGE,"E25.7");var subQ1=sQuery(id+"F0.wireOp",EDGE,"E25.1");var subQ2=sQuery(id+"F0.wireOp",EDGE,"E25.6");var subQ3=sQuery(id+"F0.wireOp",EDGE,"E25.5");var subQ4=sQuery(id+"F0.wireOp",EDGE,"E25.4");var subQ5=sQuery(id+"F0.wireOp",EDGE,"E25.0");var subQ6=sQuery(id+"F0.wireOp",EDGE,"E25.2");var subQ7=sQuery(id+"F0.wireOp",EDGE,"E25.3");Q4=makeQuery(id+"F8.boolean.opBoolean","INTERSECT",EDGE,{"derivedFrom":[makeQuery(id+"F5.boolean.opBoolean","SPLIT",FACE,{"disambiguationData":[TD([makeQuery(id+"F2.opExtrude","SWEPT_FACE",FACE,{"disambiguationData":[OSD([subQ5])]})])],"derivedFrom":makeQuery(id+"F3.boolean.opBoolean","COPY",FACE,{"derivedFrom":makeQuery(id+"F3.opExtrude","CAP_FACE",FACE,{"disambiguationData":[OSD([subQ5,subQ1,subQ6,subQ7,subQ4,subQ3,subQ2,subQ0])],"isStart":false})})}),makeQuery(id+"F8.opExtrude","SWEPT_FACE",FACE,{"disambiguationData":[OSD([sQuery(id+"F7.wireOp",EDGE,"E67")])]})]});}
            var Q5;
            Q5=makeQuery(id+"F8.boolean.opBoolean","INTERSECT",EDGE,{"disambiguationData":[OD(0.0)],"derivedFrom":[makeQuery(id+"F5.opExtrude","SWEPT_FACE",FACE,{"disambiguationData":[OSD([sQuery(id+"F4.wireOp",EDGE,"E30")])]}),makeQuery(id+"F8.opExtrude","SWEPT_FACE",FACE,{"disambiguationData":[OSD([sQuery(id+"F7.wireOp",EDGE,"E67")])]})]});
            fillet(context, id + "F14", {"entities" : qUnion([Q0, Q1, Q2, Q3, Q4, Q5]), "radius" : 3 * mm, "tangentPropagation" : true, "allowEdgeOverflow" : false});
        }
        {
            var Q0;
            Q0=makeQuery(id+"F1.opExtrude","CAP_EDGE",EDGE,{"disambiguationData":[OSD([sQuery(id+"F0.wireOp",EDGE,"E1.bottom")])],"isStart":false});
            fillet(context, id + "F15", {"entities" : qUnion([Q0]), "radius" : 2 * mm, "tangentPropagation" : true, "allowEdgeOverflow" : false});
        }
        {
            var Q0;
            {var subQ0=sQuery(id+"F0.wireOp",EDGE,"E21.filletArc");var subQ1=sQuery(id+"F0.wireOp",EDGE,"E7");var subQ2=sQuery(id+"F0.wireOp",EDGE,"E6");var subQ3=sQuery(id+"F0.wireOp",EDGE,"E5");var subQ4=sQuery(id+"F0.wireOp",EDGE,"E4");var subQ5=sQuery(id+"F0.wireOp",EDGE,"E22.filletArc");var subQ6=sQuery(id+"F0.wireOp",EDGE,"E1.bottom");var subQ7=sQuery(id+"F0.wireOp",EDGE,"E1.right");var subQ8=sQuery(id+"F0.wireOp",EDGE,"E1.top");var subQ9=sQuery(id+"F0.wireOp",EDGE,"E1.left");var subQ10=sQuery(id+"F0.wireOp",EDGE,"E23.filletArc");var subQ11=sQuery(id+"F0.wireOp",EDGE,"E24.filletArc");Q0=makeQuery(id+"F2.boolean.opBoolean","SPLIT",FACE,{"disambiguationData":[TD([makeQuery(id+"F1.opExtrude","SWEPT_FACE",FACE,{"disambiguationData":[OSD([subQ6])]})])],"derivedFrom":makeQuery(id+"F1.opExtrude","CAP_FACE",FACE,{"disambiguationData":[OSD([subQ6,subQ8,subQ9,subQ7,subQ4,subQ3,subQ2,subQ1,subQ0,subQ5,subQ10,subQ11])],"isStart":true})});}
            var sketch = newSketch(context, id + "F16", { "sketchPlane" : qUnion([Q0])});
            skLineSegment(sketch, "E79.0", {"start": v(80, -80) * mm, "end": v(80, 80) * mm});
            skLineSegment(sketch, "E79.1", {"start": v(-70, 90) * mm, "end": v(70, 90) * mm});
            skLineSegment(sketch, "E79.2", {"start": v(-80, -80) * mm, "end": v(-80, 80) * mm});
            skLineSegment(sketch, "E79.3", {"start": v(-70, -90) * mm, "end": v(70, -90) * mm});
            skArc(sketch, "E79.4", {"start": v(-70, 90) * mm, "mid": v(-77.07, 87.07) * mm, "end": v(-80, 80) * mm});
            skArc(sketch, "E79.5", {"start": v(80, 80) * mm, "mid": v(77.07, 87.07) * mm, "end": v(70, 90) * mm});
            skArc(sketch, "E79.6", {"start": v(-80, -80) * mm, "mid": v(-77.07, -87.07) * mm, "end": v(-70, -90) * mm});
            skArc(sketch, "E79.7", {"start": v(70, -90) * mm, "mid": v(77.07, -87.07) * mm, "end": v(80, -80) * mm});
            skCircle(sketch, "E79.8", {"center": v(60, -67.5) * mm, "radius": 4 * mm});
            skCircle(sketch, "E79.9", {"center": v(-60, -67.5) * mm, "radius": 4 * mm});
            skCircle(sketch, "E79.10", {"center": v(-60, 67.5) * mm, "radius": 4 * mm});
            skCircle(sketch, "E79.11", {"center": v(60, 67.5) * mm, "radius": 4 * mm});
            skArc(sketch, "E79.12", {"start": v(56.15, 48.18) * mm, "mid": v(0, 67.5) * mm, "end": v(-56.15, 48.18) * mm});
            skLineSegment(sketch, "E79.13", {"start": v(60, 40.3) * mm, "end": v(60, -40.3) * mm});
            skArc(sketch, "E79.14", {"start": v(-56.15, -48.18) * mm, "mid": v(0, -67.5) * mm, "end": v(56.15, -48.18) * mm});
            skLineSegment(sketch, "E79.15", {"start": v(-60, 40.3) * mm, "end": v(-60, -40.3) * mm});
            skArc(sketch, "E79.16", {"start": v(-56.15, 48.18) * mm, "mid": v(-58.99, 44.68) * mm, "end": v(-60, 40.3) * mm});
            skArc(sketch, "E79.17", {"start": v(-60, -40.3) * mm, "mid": v(-58.99, -44.68) * mm, "end": v(-56.15, -48.18) * mm});
            skArc(sketch, "E79.18", {"start": v(60, 40.3) * mm, "mid": v(58.99, 44.68) * mm, "end": v(56.15, 48.18) * mm});
            skArc(sketch, "E79.19", {"start": v(56.15, -48.18) * mm, "mid": v(58.99, -44.68) * mm, "end": v(60, -40.3) * mm});
            skLineSegment(sketch, "E80", {"start": v(0, 90) * mm, "end": v(0, 120) * mm, "construction": true});
            skPoint(sketch, "E80.endSnap0", {"position": v(0, 90) * mm});
            skCircle(sketch, "E81", {"center": v(0, 120) * mm, "radius": 6 * mm});
            skLineSegment(sketch, "E82", {"start": v(-33, 90) * mm, "end": v(-15, 108) * mm});
            skLineSegment(sketch, "E83", {"start": v(-15, 108) * mm, "end": v(-15, 120) * mm});
            skArc(sketch, "E84", {"start": v(15, 120) * mm, "mid": v(0, 135) * mm, "end": v(-15, 120) * mm});
            skLineSegment(sketch, "E85", {"start": v(15, 120) * mm, "end": v(15, 108) * mm});
            skLineSegment(sketch, "E86", {"start": v(15, 108) * mm, "end": v(33, 90) * mm});
            skLineSegment(sketch, "E87", {"start": v(0, 0) * mm, "end": v(-80, 0) * mm, "construction": true});
            skLineSegment(sketch, "E88", {"start": v(0, 0) * mm, "end": v(80, 0) * mm, "construction": true});
            skLineSegment(sketch, "E89.MirrorCS", {"start": v(-33, -90) * mm, "end": v(-15, -108) * mm});
            skLineSegment(sketch, "E90.MirrorCS", {"start": v(-15, -108) * mm, "end": v(-15, -120) * mm});
            skArc(sketch, "E91.MirrorCS", {"start": v(15, -120) * mm, "mid": v(0, -135) * mm, "end": v(-15, -120) * mm});
            skCircle(sketch, "E92.MirrorC", {"center": v(0, -120) * mm, "radius": 6 * mm});
            skLineSegment(sketch, "E93.MirrorCS", {"start": v(15, -120) * mm, "end": v(15, -108) * mm});
            skLineSegment(sketch, "E94.MirrorCS", {"start": v(15, -108) * mm, "end": v(33, -90) * mm});
            skSolve(sketch);
        }
        {
            var Q0;
            Q0 = qSketchRegion(id + "F16", true);
            var Q1;
            {var subQ0=sQuery(id+"F4.wireOp",EDGE,"E36.filletArc");var subQ1=sQuery(id+"F4.wireOp",EDGE,"E35.filletArc");var subQ2=sQuery(id+"F4.wireOp",EDGE,"E34.filletArc");var subQ3=sQuery(id+"F4.wireOp",EDGE,"E33.filletArc");var subQ4=sQuery(id+"F4.wireOp",EDGE,"E27.0");var subQ5=sQuery(id+"F4.wireOp",EDGE,"E30");var subQ6=sQuery(id+"F4.wireOp",EDGE,"E28.0");var subQ7=sQuery(id+"F4.wireOp",EDGE,"E29");Q1=makeQuery(id+"F6.boolean.opBoolean","SPLIT",FACE,{"disambiguationData":[TD([makeQuery(id+"F5.opExtrude","SWEPT_FACE",FACE,{"disambiguationData":[OSD([subQ4])]})])],"derivedFrom":makeQuery(id+"F5.opExtrude","CAP_FACE",FACE,{"disambiguationData":[OSD([subQ4,subQ6,subQ7,subQ5,subQ3,subQ2,subQ1,subQ0,sQuery(id+"F4.wireOp",EDGE,"E41"),sQuery(id+"F4.wireOp",EDGE,"E42"),sQuery(id+"F4.wireOp",EDGE,"E43"),sQuery(id+"F4.wireOp",EDGE,"E45"),sQuery(id+"F4.wireOp",EDGE,"E46"),sQuery(id+"F4.wireOp",EDGE,"E47.filletArc"),sQuery(id+"F4.wireOp",EDGE,"E48.filletArc"),sQuery(id+"F4.wireOp",EDGE,"E49.filletArc"),sQuery(id+"F4.wireOp",EDGE,"E50.filletArc"),sQuery(id+"F4.wireOp",EDGE,"E51.filletArc"),sQuery(id+"F4.wireOp",EDGE,"E52.filletArc"),sQuery(id+"F4.wireOp",EDGE,"E53.0.MirrorCS"),sQuery(id+"F4.wireOp",EDGE,"E54.0.MirrorCS"),sQuery(id+"F4.wireOp",EDGE,"E55.0.MirrorCS"),sQuery(id+"F4.wireOp",EDGE,"E56.0.MirrorCS"),sQuery(id+"F4.wireOp",EDGE,"E57.0.MirrorCS"),sQuery(id+"F4.wireOp",EDGE,"E58.0.MirrorCS"),sQuery(id+"F4.wireOp",EDGE,"E59.0.MirrorCS"),sQuery(id+"F4.wireOp",EDGE,"E60.0.MirrorCS"),sQuery(id+"F4.wireOp",EDGE,"E61.0.MirrorCS"),sQuery(id+"F4.wireOp",EDGE,"E62.0.MirrorCS"),sQuery(id+"F4.wireOp",EDGE,"E63.0.MirrorCS")])],"isStart":true})});}
            extrude(context, id + "F17", {"entities" : qUnion([Q0]), "endBound" : BoundingType.UP_TO_SURFACE, "endBoundEntityFace" : qUnion([Q1]), "depth" : 25 * mm});
        }
    });
